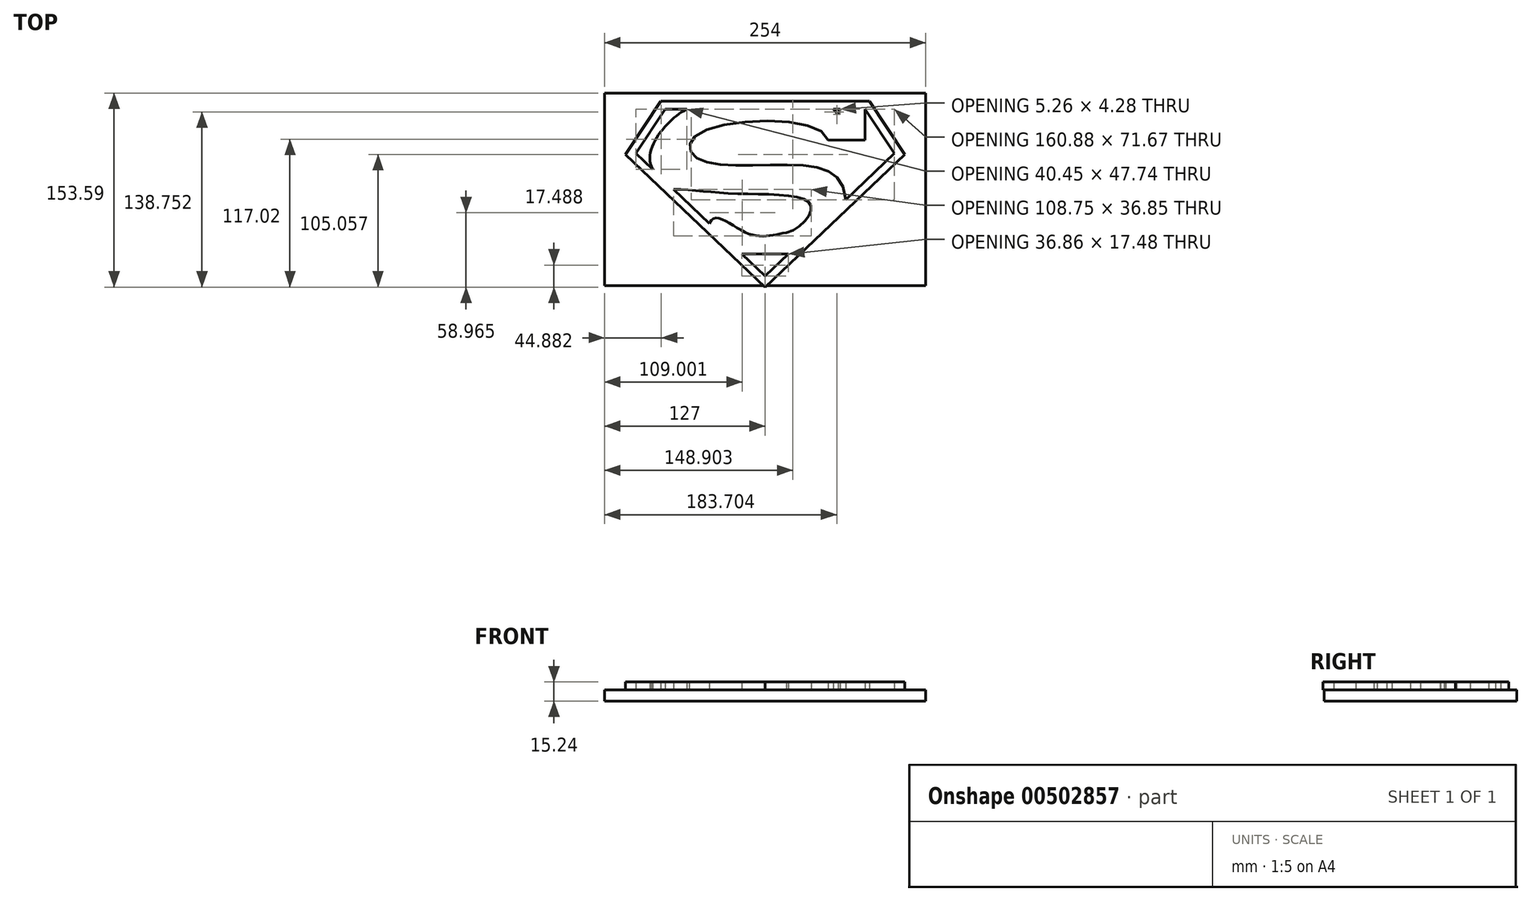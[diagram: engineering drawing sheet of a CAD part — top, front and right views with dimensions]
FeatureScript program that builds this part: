
annotation { "Feature Type Name" : "Feature", "Feature Type Description" : "" }
export const myFeature = defineFeature(function(context is Context, id is Id, definition is map)
    precondition{}
    {
        {
            var Q0;
            Q0=qCreatedBy(makeId("Top.planeOp"),FACE);
            var sketch = newSketch(context, id + "F0", { "sketchPlane" : qUnion([Q0])});
            skLineSegment(sketch, "E0.bottom", {"start": v(127, 76.2) * mm, "end": v(-127, 76.2) * mm});
            skLineSegment(sketch, "E0.top", {"start": v(127, -76.2) * mm, "end": v(-127, -76.2) * mm});
            skLineSegment(sketch, "E0.left", {"start": v(127, 76.2) * mm, "end": v(127, -76.2) * mm});
            skLineSegment(sketch, "E0.right", {"start": v(-127, 76.2) * mm, "end": v(-127, -76.2) * mm});
            skSolve(sketch);
        }
        {
            var Q0;
            Q0 = qSketchRegion(id + "F0", true);
            extrude(context, id + "F1", {"entities" : qUnion([Q0]), "oppositeDirection" : true, "depth" : 8.9 * mm});
        }
        {
            var Q0;
            Q0=makeQuery(id+"F1.opExtrude","CAP_FACE",FACE,{"disambiguationData":[OSD([sQuery(id+"F0.wireOp",EDGE,"E0.bottom"),sQuery(id+"F0.wireOp",EDGE,"E0.top"),sQuery(id+"F0.wireOp",EDGE,"E0.left"),sQuery(id+"F0.wireOp",EDGE,"E0.right")])],"isStart":true});
            var sketch = newSketch(context, id + "F2", { "sketchPlane" : qUnion([Q0])});
            skLineSegment(sketch, "E1", {"start": v(0, -77.4) * mm, "end": v(-110.58, 27.48) * mm});
            skLineSegment(sketch, "E2", {"start": v(-110.58, 27.48) * mm, "end": v(-82.55, 69.85) * mm});
            skLineSegment(sketch, "E3", {"start": v(-82.55, 69.85) * mm, "end": v(0, 69.85) * mm});
            skLineSegment(sketch, "E4", {"start": v(0, -69.85) * mm, "end": v(0, 69.85) * mm, "construction": true});
            skLineSegment(sketch, "E5.MirrorCS", {"start": v(82.55, 69.85) * mm, "end": v(0, 69.85) * mm});
            skLineSegment(sketch, "E6.MirrorCS", {"start": v(110.58, 27.48) * mm, "end": v(82.55, 69.85) * mm});
            skLineSegment(sketch, "E7.MirrorCS", {"start": v(0, -77.4) * mm, "end": v(110.58, 27.48) * mm});
            skLineSegment(sketch, "E8.0", {"start": v(-79.14, 63.5) * mm, "end": v(0, 63.5) * mm});
            skLineSegment(sketch, "E8.1", {"start": v(-102.34, 28.42) * mm, "end": v(-79.14, 63.5) * mm});
            skLineSegment(sketch, "E8.2", {"start": v(0, -68.64) * mm, "end": v(-102.34, 28.42) * mm});
            skLineSegment(sketch, "E9.0", {"start": v(79.14, 63.5) * mm, "end": v(0.5, 63.5) * mm});
            skLineSegment(sketch, "E9.1", {"start": v(102.34, 28.42) * mm, "end": v(79.14, 63.5) * mm});
            skLineSegment(sketch, "E9.2", {"start": v(0, -68.64) * mm, "end": v(102.34, 28.42) * mm});
            skLineSegment(sketch, "E10", {"start": v(-18.43, -51.16) * mm, "end": v(18.43, -51.16) * mm});
            skLineSegment(sketch, "E11", {"start": v(79.14, 63.5) * mm, "end": v(79.14, 39.13) * mm});
            skLineSegment(sketch, "E12", {"start": v(79.14, 39.13) * mm, "end": v(49.71, 39.13) * mm});
            skLineSegment(sketch, "E13", {"start": v(59.34, 63.5) * mm, "end": v(57.64, 59.22) * mm});
            skLineSegment(sketch, "E14", {"start": v(57.64, 59.22) * mm, "end": v(54.07, 63.5) * mm});
            skLineSegment(sketch, "E15", {"start": v(54.07, 63.5) * mm, "end": v(59.34, 63.5) * mm});
            skFitSpline(sketch, "E16", {"points": [v(-61.9, 63.5) * mm, v(-89, 15.76) * mm], "startDerivative": vector(-34.7, -15.96) * mm, "endDerivative": vector(29.01, -54.67) * mm});
            skFitSpline(sketch, "E17", {"points": [v(49.71, 39.13) * mm, v(-53.41, 43.53) * mm, v(-53.8, 24.64) * mm, v(30.23, 18.86) * mm, v(63.76, -8.17) * mm], "startDerivative": vector(-42.16, 179.78) * mm, "endDerivative": vector(21.65, -272.3) * mm});
            skFitSpline(sketch, "E18", {"points": [v(-72.37, 0) * mm, v(-19.39, -3.5) * mm, v(36.02, -12.37) * mm, v(16.74, -34.35) * mm], "startDerivative": vector(132.1, -1.35) * mm, "endDerivative": vector(-126.25, -30.09) * mm});
            skPoint(sketch, "E19.1.internal.orphan", {"position": v(-19.39, 0) * mm});
            skFitSpline(sketch, "E20", {"points": [v(16.74, -34.35) * mm, v(-14.87, -34.35) * mm, v(-44, -26.91) * mm], "startDerivative": vector(-61.68, -9.14) * mm, "endDerivative": vector(-27.11, -67.26) * mm});
            skLineSegment(sketch, "E21", {"start": v(-90.56, 19.78) * mm, "end": v(-89, 15.76) * mm});
            skSolve(sketch);
        }
        {
            var Q0;
            Q0 = qSketchRegion(id + "F2", true);
            extrude(context, id + "F3", {"entities" : qUnion([Q0]), "depth" : 6.35 * mm});
        }
        {
            var Q0;
            {var subQ1=sQuery(id+"F2.wireOp",EDGE,"E9.1");Q0=makeQuery(id+"F2.imprint","IMPRINT",FACE,{"disambiguationData":[TD([[makeQuery(id+"F2.imprint","IMPRINT",EDGE,{"derivedFrom":subQ1}),1.0]])]});}
            var Q1;
            {var subQ0=sQuery(id+"F2.wireOp",EDGE,"E18");Q1=makeQuery(id+"F2.imprint","IMPRINT",FACE,{"disambiguationData":[TD([[makeQuery(id+"F2.imprint","IMPRINT",EDGE,{"derivedFrom":subQ0}),-1.0]])]});}
            var Q2;
            {var subQ3=sQuery(id+"F2.wireOp",EDGE,"E10");Q2=makeQuery(id+"F2.imprint","IMPRINT",FACE,{"disambiguationData":[TD([[makeQuery(id+"F2.imprint","IMPRINT",EDGE,{"derivedFrom":subQ3}),-1.0]])]});}
            var Q3;
            {var subQ2=sQuery(id+"F2.wireOp",EDGE,"E8.1");Q3=makeQuery(id+"F2.imprint","IMPRINT",FACE,{"disambiguationData":[TD([[makeQuery(id+"F2.imprint","IMPRINT",EDGE,{"derivedFrom":subQ2}),-1.0]])]});}
            var Q4;
            Q4=makeQuery(id+"F2.imprint","IMPRINT",FACE,{"disambiguationData":[TD([[makeQuery(id+"F2.imprint","IMPRINT",EDGE,{"derivedFrom":sQuery(id+"F2.wireOp",EDGE,"E13")}),-1.0]])]});
            var Q5;
            Q5=makeQuery(id+"F3.opExtrude","CAP_FACE",FACE,{"disambiguationData":[OSD([sQuery(id+"F2.wireOp",EDGE,"E1"),sQuery(id+"F2.wireOp",EDGE,"E2"),sQuery(id+"F2.wireOp",EDGE,"E3"),sQuery(id+"F2.wireOp",EDGE,"E5.MirrorCS"),sQuery(id+"F2.wireOp",EDGE,"E6.MirrorCS"),sQuery(id+"F2.wireOp",EDGE,"E7.MirrorCS"),sQuery(id+"F2.wireOp",EDGE,"E8.0"),sQuery(id+"F2.wireOp",EDGE,"E8.1"),sQuery(id+"F2.wireOp",EDGE,"E8.2"),sQuery(id+"F2.wireOp",EDGE,"E9.1"),sQuery(id+"F2.wireOp",EDGE,"E9.2"),sQuery(id+"F2.wireOp",EDGE,"E10"),sQuery(id+"F2.wireOp",EDGE,"E11"),sQuery(id+"F2.wireOp",EDGE,"E12"),sQuery(id+"F2.wireOp",EDGE,"E13"),sQuery(id+"F2.wireOp",EDGE,"E14"),sQuery(id+"F2.wireOp",EDGE,"E15"),sQuery(id+"F2.wireOp",EDGE,"E16"),sQuery(id+"F2.wireOp",EDGE,"E17"),sQuery(id+"F2.wireOp",EDGE,"E18"),sQuery(id+"F2.wireOp",EDGE,"E20"),sQuery(id+"F2.wireOp",EDGE,"E21")])],"isStart":false});
            extrude(context, id + "F4", {"entities" : qUnion([Q0, Q1, Q2, Q3, Q4]), "endBound" : BoundingType.UP_TO_SURFACE, "depth" : 25.4 * mm, "endBoundEntityFace" : qUnion([Q5]), "offsetDistance" : 25.4 * mm});
        }
    });
